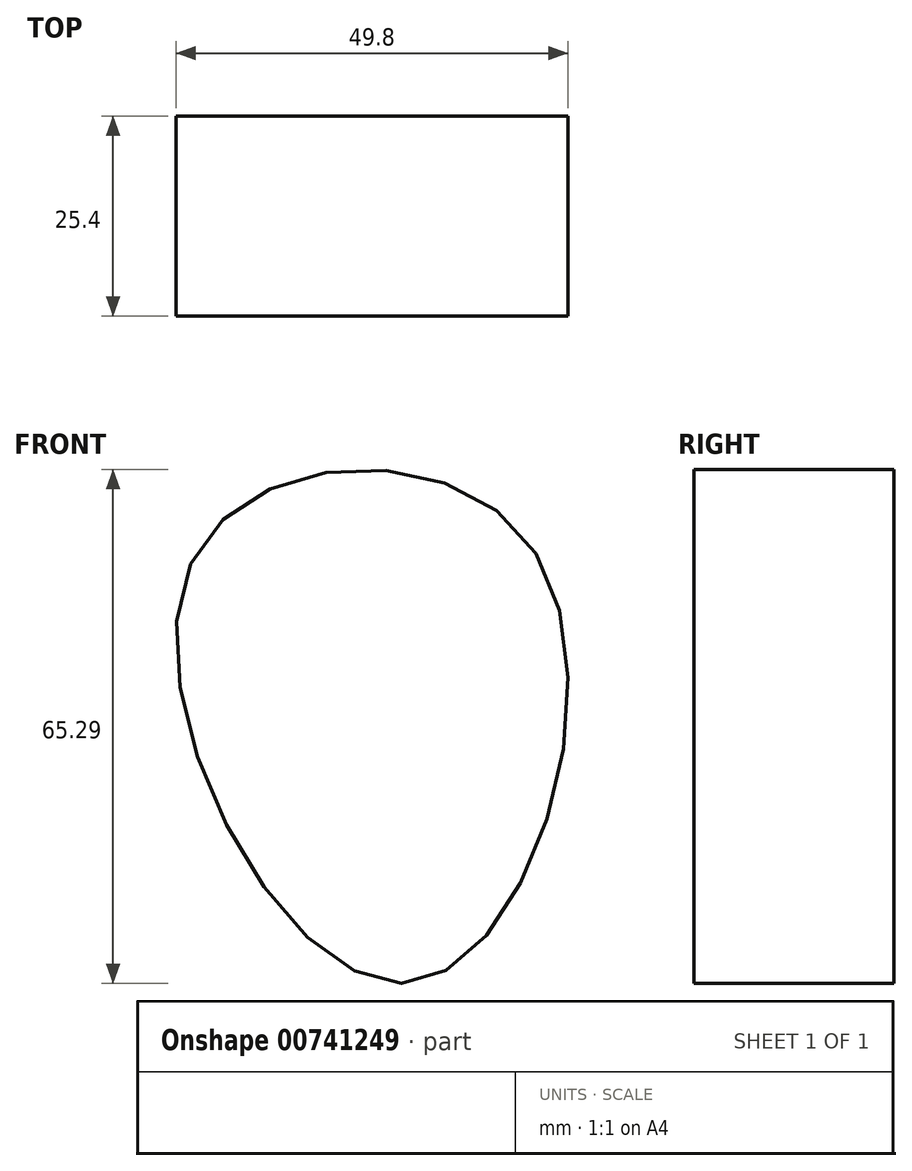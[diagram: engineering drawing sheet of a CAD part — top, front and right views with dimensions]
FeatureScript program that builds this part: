
annotation { "Feature Type Name" : "Feature", "Feature Type Description" : "" }
export const myFeature = defineFeature(function(context is Context, id is Id, definition is map)
    precondition{}
    {
        {
            var Q0;
            Q0=qCreatedBy(makeId("Front.planeOp"),FACE);
            var sketch = newSketch(context, id + "F0", { "sketchPlane" : qUnion([Q0])});
            skFitSpline(sketch, "E0", {"points": [v(-56.7, 31.98) * mm, v(-13.12, 33.76) * mm, v(-29.18, -21.28) * mm, v(-56.7, 31.98) * mm]});
            skSolve(sketch);
        }
        {
            var Q0;
            Q0=makeQuery(id+"F0.imprint","IMPRINT",FACE,{"disambiguationData":[TD([[makeQuery(id+"F0.imprint","IMPRINT",EDGE,{"derivedFrom":sQuery(id+"F0.wireOp",EDGE,"E0")}),-1.0]])]});
            extrude(context, id + "F1", {"entities" : qUnion([Q0]), "depth" : 25.4 * mm, "offsetDistance" : 25.4 * mm});
        }
    });
